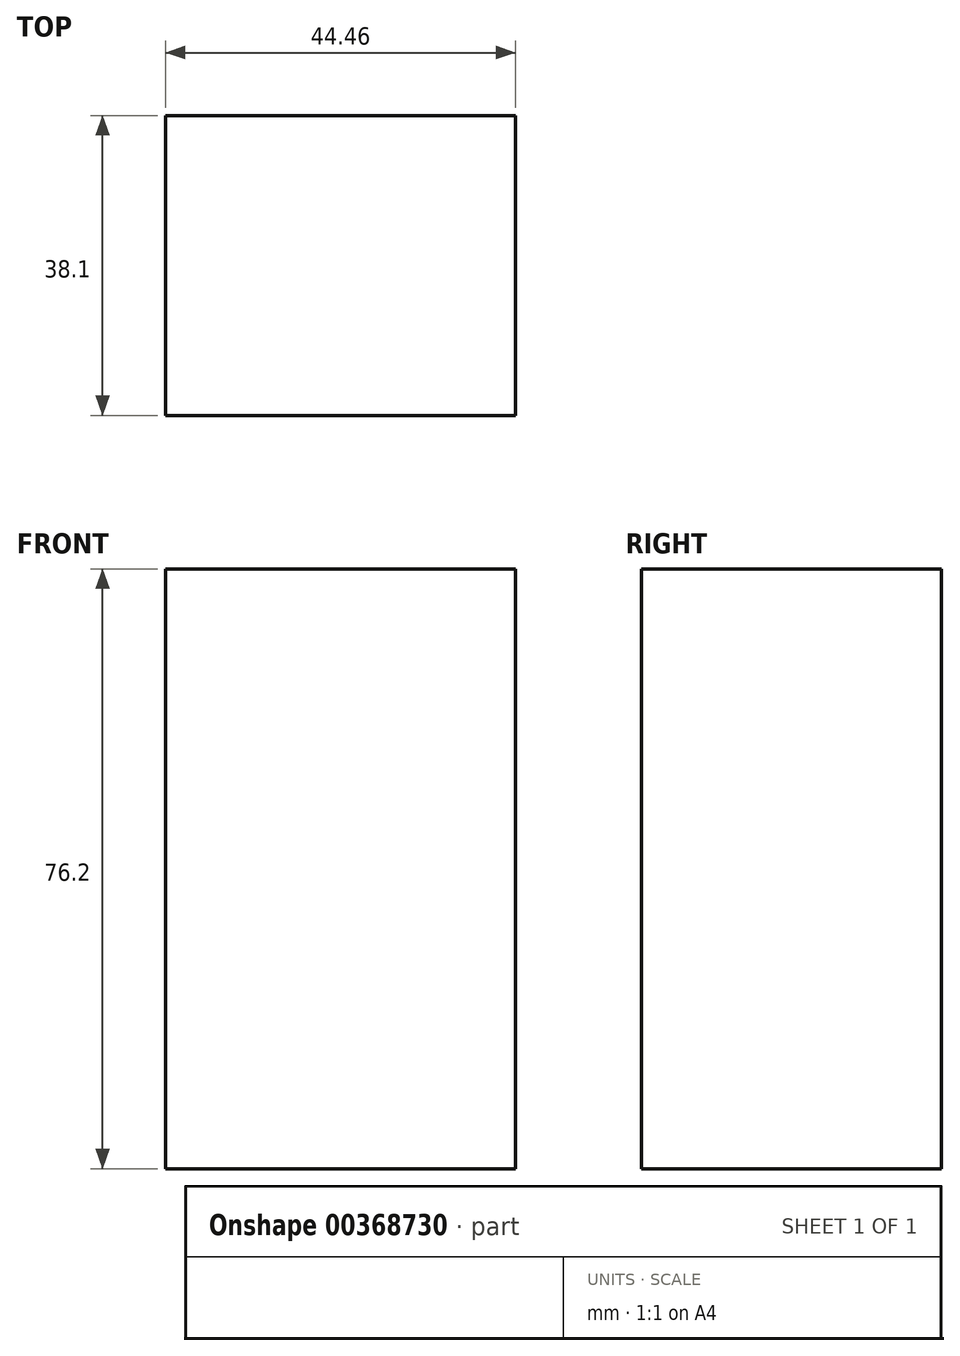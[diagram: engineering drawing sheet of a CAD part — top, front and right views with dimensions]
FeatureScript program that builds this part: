
annotation { "Feature Type Name" : "Feature", "Feature Type Description" : "" }
export const myFeature = defineFeature(function(context is Context, id is Id, definition is map)
    precondition{}
    {
        {
            var Q0;
            Q0=qCreatedBy(makeId("Top.planeOp"),FACE);
            var sketch = newSketch(context, id + "F0", { "sketchPlane" : qUnion([Q0])});
            skLineSegment(sketch, "E0.bottom", {"start": v(22.23, 19.05) * mm, "end": v(-22.23, 19.05) * mm});
            skLineSegment(sketch, "E0.top", {"start": v(22.23, -19.05) * mm, "end": v(-22.22, -19.05) * mm});
            skLineSegment(sketch, "E0.left", {"start": v(22.23, 19.05) * mm, "end": v(22.23, -19.05) * mm});
            skLineSegment(sketch, "E0.right", {"start": v(-22.22, 19.05) * mm, "end": v(-22.22, -19.05) * mm});
            skPoint(sketch, "E0.middle", {"position": v(0, 0) * mm});
            skSolve(sketch);
        }
        {
            var Q0;
            Q0=makeQuery(id+"F0.imprint","IMPRINT",FACE,{"disambiguationData":[TD([[makeQuery(id+"F0.imprint","IMPRINT",EDGE,{"derivedFrom":sQuery(id+"F0.wireOp",EDGE,"E0.bottom")}),1.0]])]});
            extrude(context, id + "F1", {"entities" : qUnion([Q0]), "depth" : 76.2 * mm});
        }
    });
